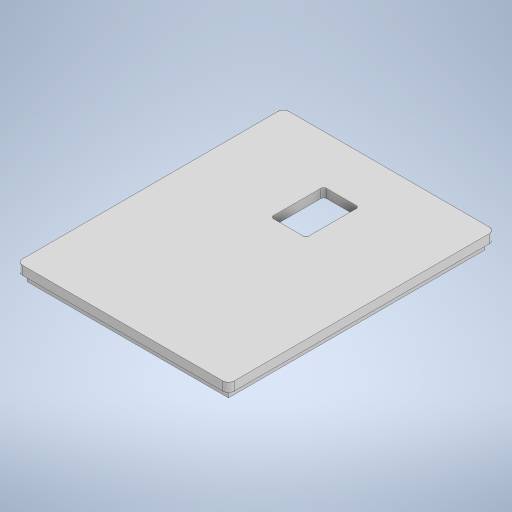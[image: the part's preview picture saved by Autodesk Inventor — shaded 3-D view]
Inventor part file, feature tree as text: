
AUTODESK INVENTOR PART (.ipt)
format: ipt  version: 2024.2 (Build 282272000, 272)  size: 422,400 bytes
history: native  units: in
note: dims shown in document units (in); Inventor stores cm internally (conversion verified against a paired STEP export)
features: extrude x3, sketch x3, fillet x2, projected_geometry x2
ambient origin geometry x8: Origin, YZ Plane, XZ Plane, XY Plane, X Axis, Y Axis, Z Axis, Center Point
bodies: Solid1 (feature_tree)
feature tree (10):
  extrude  "Extrusion1"  Depth=0.75in
  fillet  "Fillet1"  Radius=0.0312in
  extrude  "Extrusion2"  Depth=0.018in
  extrude  "Extrusion3"  Depth=0.018in
  fillet  "Fillet2"  Radius=0.018in
  sketch  "Sketch1"  dims[d0=0.945in d1=0.75in d2=0.0312in d3=0.0in]
  sketch  "Sketch2"  dims[d4=0.02in d5=0.018in]
  projected_geometry  "Projected Loop1"
  sketch  "Sketch3"  dims[d6=0.018in d7=0.018in d8=0.018in d9=0.045in d10=0.045in d11=0.045in d12=0.045in d13=0.029in d14=0.0in d15=0.125in d16=0.1875in d17=0.75in d18=0.3125in d19=0.3125in d20=0.17in d21=0.154in d22=0.0in d23=0.01in d24=0.0344in]
  projected_geometry  "Projected Loop2"
